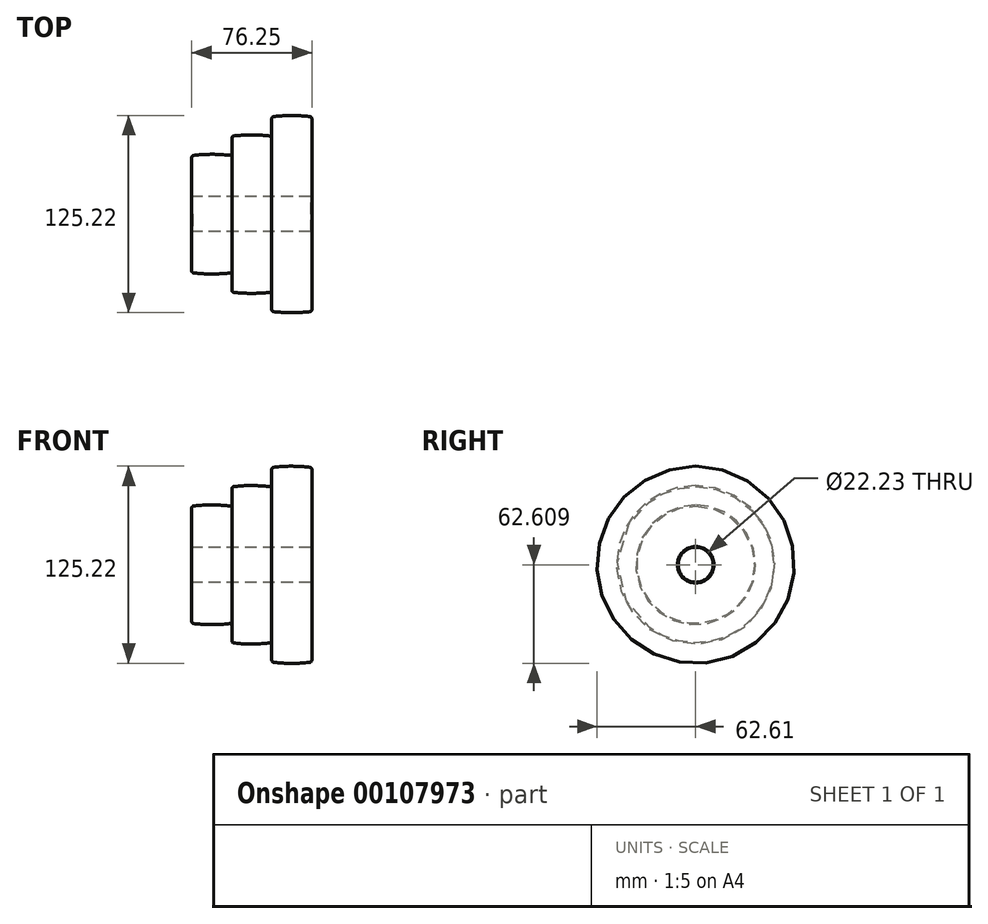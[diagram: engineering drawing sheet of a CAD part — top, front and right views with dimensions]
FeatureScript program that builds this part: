
annotation { "Feature Type Name" : "Feature", "Feature Type Description" : "" }
export const myFeature = defineFeature(function(context is Context, id is Id, definition is map)
    precondition{}
    {
        {
            var Q0;
            Q0=qCreatedBy(makeId("Front.planeOp"),FACE);
            var sketch = newSketch(context, id + "F0", { "sketchPlane" : qUnion([Q0])});
            skLineSegment(sketch, "E0", {"start": v(-239.3, -11.81) * mm, "end": v(166.27, -11.81) * mm, "construction": true});
            skLineSegment(sketch, "E1", {"start": v(0, -0.7) * mm, "end": v(76.25, -0.7) * mm});
            skLineSegment(sketch, "E2", {"start": v(76.25, -0.7) * mm, "end": v(76.25, 48.87) * mm});
            skLineSegment(sketch, "E3", {"start": v(50.85, 48.93) * mm, "end": v(50.85, 39.12) * mm});
            skLineSegment(sketch, "E4", {"start": v(25.54, 36.6) * mm, "end": v(25.54, 26.95) * mm});
            skLineSegment(sketch, "E5", {"start": v(0, 24.27) * mm, "end": v(0, -0.7) * mm});
            skPoint(sketch, "E6.second.point", {"position": v(12.7, 27.16) * mm});
            skPoint(sketch, "E6.second.point.positionSnap0", {"position": v(12.7, 25.4) * mm});
            skPoint(sketch, "E7.second.point", {"position": v(37.98, 38.5) * mm});
            skPoint(sketch, "E8.second.point.positionSnap0", {"position": v(63.5, 50.8) * mm});
            skArc(sketch, "E9.trimOffspring", {"start": v(23.99, 25.57) * mm, "mid": v(12.56, 26.2) * mm, "end": v(1.13, 25.54) * mm});
            skArc(sketch, "E10.trimOffspring", {"start": v(75.13, 50.13) * mm, "mid": v(63.53, 50.8) * mm, "end": v(51.93, 50.14) * mm});
            skPoint(sketch, "E11.visualSharp", {"position": v(0, 25.4) * mm});
            skArc(sketch, "E11.filletArc", {"start": v(1.13, 25.54) * mm, "mid": v(0.32, 25.12) * mm, "end": v(0, 24.27) * mm});
            skPoint(sketch, "E12.visualSharp", {"position": v(25.54, 25.38) * mm});
            skArc(sketch, "E12.filletArc", {"start": v(23.99, 25.57) * mm, "mid": v(25.07, 25.91) * mm, "end": v(25.54, 26.95) * mm});
            skPoint(sketch, "E13.visualSharp", {"position": v(25.54, 38.08) * mm});
            skPoint(sketch, "E14.visualSharp", {"position": v(50.85, 37.3) * mm});
            skPoint(sketch, "E15.visualSharp", {"position": v(50.85, 50) * mm});
            skArc(sketch, "E15.filletArc", {"start": v(51.93, 50.14) * mm, "mid": v(51.16, 49.74) * mm, "end": v(50.85, 48.93) * mm});
            skPoint(sketch, "E16.visualSharp", {"position": v(76.25, 50) * mm});
            skArc(sketch, "E16.filletArc", {"start": v(76.25, 48.87) * mm, "mid": v(75.93, 49.72) * mm, "end": v(75.13, 50.13) * mm});
            skPoint(sketch, "E17.third.point", {"position": v(12.7, 26.2) * mm});
            skLineSegment(sketch, "E18", {"start": v(50.68, -50.8) * mm, "end": v(79.71, -50.8) * mm, "construction": true});
            skArc(sketch, "E19.trimOffspring", {"start": v(49.44, 37.85) * mm, "mid": v(38.05, 38.5) * mm, "end": v(26.67, 37.87) * mm});
            skArc(sketch, "E20.filletArc", {"start": v(26.67, 37.87) * mm, "mid": v(25.86, 37.46) * mm, "end": v(25.54, 36.6) * mm});
            skArc(sketch, "E21.filletArc", {"start": v(49.44, 37.85) * mm, "mid": v(50.43, 38.17) * mm, "end": v(50.85, 39.12) * mm});
            skSolve(sketch);
        }
        {
            var Q0;
            Q0=makeQuery(id+"F0.imprint","IMPRINT",FACE,{"disambiguationData":[TD([[makeQuery(id+"F0.imprint","IMPRINT",EDGE,{"derivedFrom":sQuery(id+"F0.wireOp",EDGE,"E1")}),1.0]])]});
            var Q1;
            Q1=sQuery(id+"F0.wireOp",EDGE,"E0");
            revolve(context, id + "F1", {"entities" : qUnion([Q0]), "axis" : qUnion([Q1]), "revolveType" : RevolveType.FULL});
        }
        {
            var Q0;
            Q0=makeQuery(id+"F1.opRevolve","SWEPT_EDGE",EDGE,{"disambiguationData":[OSD([sQuery(id+"F0.wireOp",EDGE,"E1"),sQuery(id+"F0.wireOp",EDGE,"E2")])]});
            var Q1;
            Q1=makeQuery(id+"F1.opRevolve","SWEPT_EDGE",EDGE,{"disambiguationData":[OSD([sQuery(id+"F0.wireOp",EDGE,"E1"),sQuery(id+"F0.wireOp",EDGE,"E5")])]});
            chamfer(context, id + "F2", {"entities" : qUnion([Q0, Q1]), "width" : 0.5 * mm, "tangentPropagation" : true});
        }
    });
